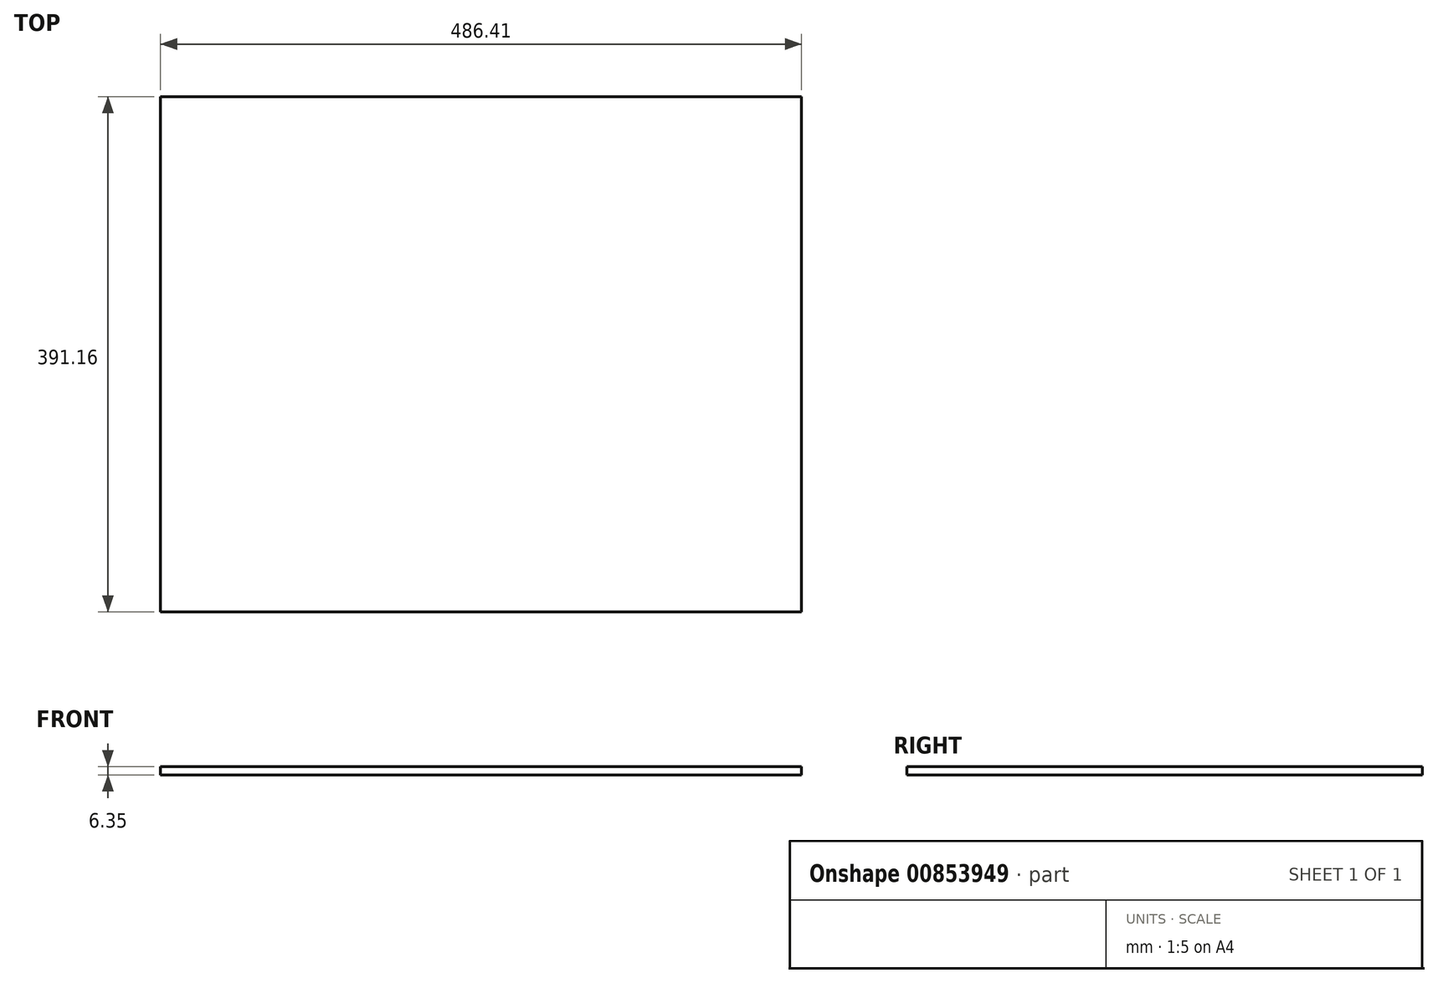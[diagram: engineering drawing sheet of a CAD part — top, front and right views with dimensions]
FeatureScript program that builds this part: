
annotation { "Feature Type Name" : "Feature", "Feature Type Description" : "" }
export const myFeature = defineFeature(function(context is Context, id is Id, definition is map)
    precondition{}
    {
        {
            var Q0;
            Q0=qCreatedBy(makeId("Top.planeOp"),FACE);
            var sketch = newSketch(context, id + "F0", { "sketchPlane" : qUnion([Q0])});
            skLineSegment(sketch, "E0.bottom", {"start": v(0, 391.16) * mm, "end": v(486.41, 391.16) * mm});
            skLineSegment(sketch, "E0.top", {"start": v(0, 0) * mm, "end": v(486.41, 0) * mm});
            skLineSegment(sketch, "E0.left", {"start": v(0, 391.16) * mm, "end": v(0, 0) * mm});
            skLineSegment(sketch, "E0.right", {"start": v(486.41, 391.16) * mm, "end": v(486.41, 0) * mm});
            skSolve(sketch);
        }
        {
            var Q0;
            Q0=makeQuery(id+"F0.imprint","IMPRINT",FACE,{"disambiguationData":[TD([[makeQuery(id+"F0.imprint","IMPRINT",EDGE,{"derivedFrom":sQuery(id+"F0.wireOp",EDGE,"E0.bottom")}),-1.0]])]});
            extrude(context, id + "F1", {"entities" : qUnion([Q0]), "depth" : 6.35 * mm, "offsetDistance" : 25.4 * mm});
        }
    });
